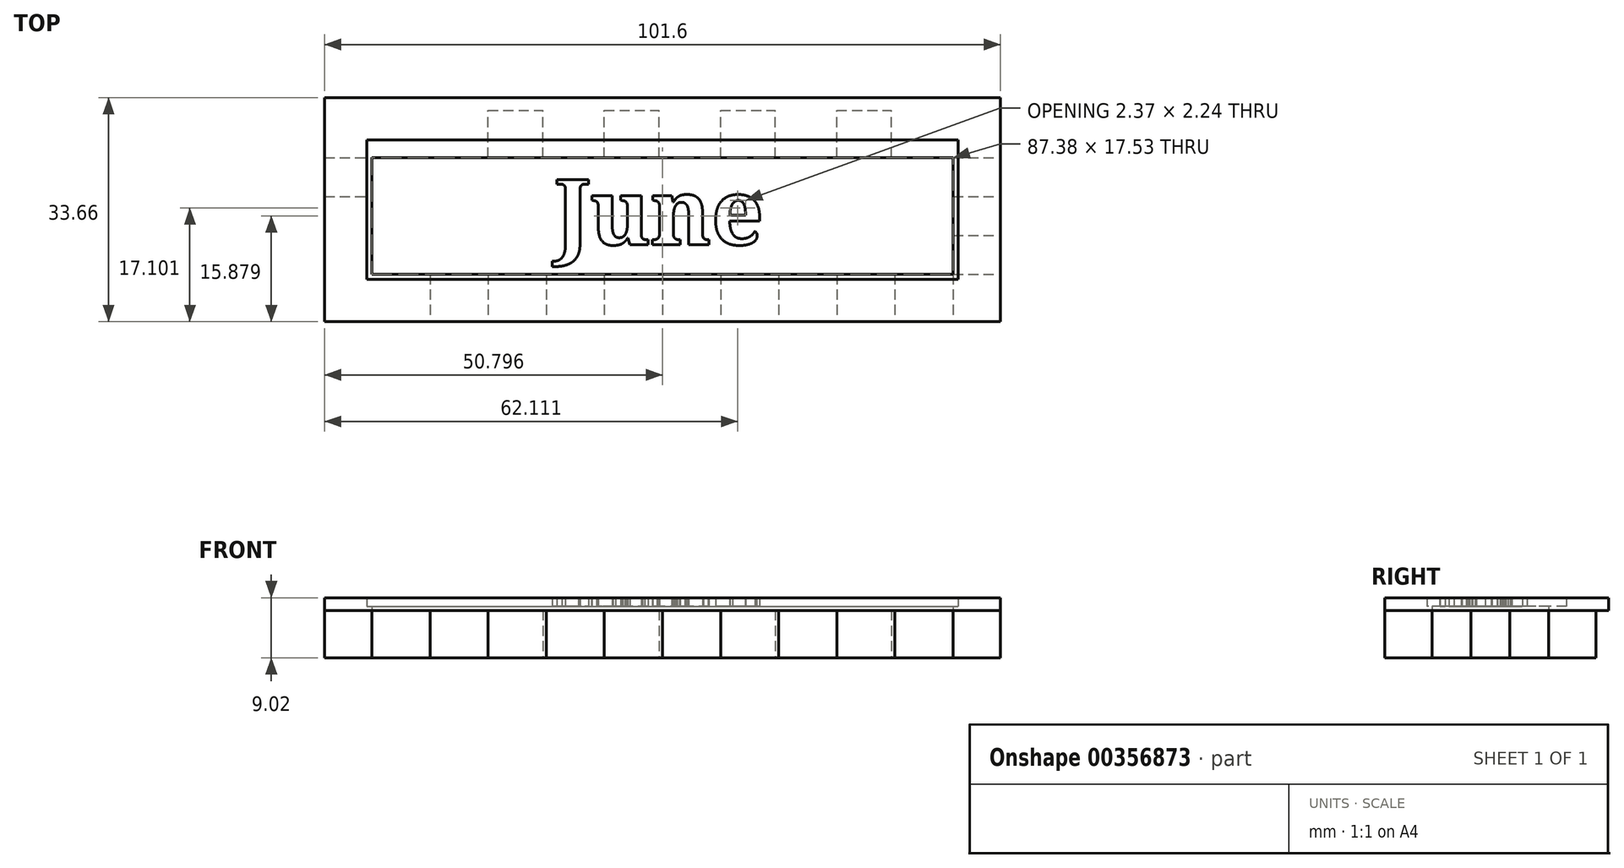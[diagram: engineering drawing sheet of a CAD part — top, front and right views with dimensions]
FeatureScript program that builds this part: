
annotation { "Feature Type Name" : "Feature", "Feature Type Description" : "" }
export const myFeature = defineFeature(function(context is Context, id is Id, definition is map)
    precondition{}
    {
        {
            var Q0;
            Q0=qCreatedBy(makeId("Top.planeOp"),FACE);
            var sketch = newSketch(context, id + "F0", { "sketchPlane" : qUnion([Q0])});
            skLineSegment(sketch, "E0.bottom", {"start": v(-52.12, 11.37) * mm, "end": v(49.48, 11.37) * mm});
            skLineSegment(sketch, "E0.top", {"start": v(-52.12, -20.38) * mm, "end": v(49.48, -20.38) * mm});
            skLineSegment(sketch, "E0.left", {"start": v(-52.12, 11.37) * mm, "end": v(-52.12, -20.38) * mm});
            skLineSegment(sketch, "E0.right", {"start": v(49.48, 11.37) * mm, "end": v(49.48, -20.38) * mm});
            skLineSegment(sketch, "E1.bottom", {"start": v(-52.12, 11.37) * mm, "end": v(-45.01, 11.37) * mm});
            skLineSegment(sketch, "E1.top", {"start": v(-52.12, 4.26) * mm, "end": v(-45.01, 4.26) * mm});
            skLineSegment(sketch, "E1.left", {"start": v(-52.12, 11.37) * mm, "end": v(-52.12, 4.26) * mm});
            skLineSegment(sketch, "E1.right", {"start": v(-45.01, 11.37) * mm, "end": v(-45.01, 4.26) * mm});
            skLineSegment(sketch, "E2.bottom", {"start": v(-45.01, 11.37) * mm, "end": v(-36.78, 11.37) * mm});
            skLineSegment(sketch, "E2.top", {"start": v(-45.01, 4.26) * mm, "end": v(-36.78, 4.26) * mm});
            skLineSegment(sketch, "E2.right", {"start": v(-36.78, 11.37) * mm, "end": v(-36.78, 4.26) * mm});
            skLineSegment(sketch, "E3.bottom", {"start": v(-36.78, 4.26) * mm, "end": v(-27.54, 4.26) * mm});
            skLineSegment(sketch, "E3.top", {"start": v(-36.78, 11.37) * mm, "end": v(-27.54, 11.37) * mm});
            skLineSegment(sketch, "E3.left", {"start": v(-36.78, 4.26) * mm, "end": v(-36.78, 11.37) * mm});
            skLineSegment(sketch, "E3.right", {"start": v(-27.54, 4.26) * mm, "end": v(-27.54, 11.37) * mm});
            skLineSegment(sketch, "E4.bottom", {"start": v(-27.54, 4.26) * mm, "end": v(-19.3, 4.26) * mm});
            skLineSegment(sketch, "E4.top", {"start": v(-27.54, 11.37) * mm, "end": v(-19.3, 11.37) * mm});
            skLineSegment(sketch, "E4.right", {"start": v(-19.3, 4.26) * mm, "end": v(-19.3, 11.37) * mm});
            skLineSegment(sketch, "E5.bottom", {"start": v(-19.3, 4.26) * mm, "end": v(-10.06, 4.26) * mm});
            skLineSegment(sketch, "E5.top", {"start": v(-19.3, 11.37) * mm, "end": v(-10.06, 11.37) * mm});
            skLineSegment(sketch, "E5.right", {"start": v(-10.06, 4.26) * mm, "end": v(-10.06, 11.37) * mm});
            skLineSegment(sketch, "E6.bottom", {"start": v(-10.06, 4.26) * mm, "end": v(-10.06, 4.26) * mm});
            skLineSegment(sketch, "E6.top", {"start": v(-10.06, 11.37) * mm, "end": v(-10.06, 11.37) * mm});
            skLineSegment(sketch, "E7.bottom", {"start": v(-10.06, 4.26) * mm, "end": v(-1.83, 4.26) * mm});
            skLineSegment(sketch, "E7.top", {"start": v(-10.06, 11.37) * mm, "end": v(-1.83, 11.37) * mm});
            skLineSegment(sketch, "E7.right", {"start": v(-1.83, 4.26) * mm, "end": v(-1.83, 11.37) * mm});
            skLineSegment(sketch, "E8.bottom", {"start": v(-1.83, 4.26) * mm, "end": v(7.41, 4.26) * mm});
            skLineSegment(sketch, "E8.top", {"start": v(-1.83, 11.37) * mm, "end": v(7.41, 11.37) * mm});
            skLineSegment(sketch, "E8.right", {"start": v(7.41, 4.26) * mm, "end": v(7.41, 11.37) * mm});
            skLineSegment(sketch, "E9.bottom", {"start": v(7.41, 4.26) * mm, "end": v(15.64, 4.26) * mm});
            skLineSegment(sketch, "E9.top", {"start": v(7.41, 11.37) * mm, "end": v(15.64, 11.37) * mm});
            skLineSegment(sketch, "E9.right", {"start": v(15.64, 4.26) * mm, "end": v(15.64, 11.37) * mm});
            skLineSegment(sketch, "E10.bottom", {"start": v(15.64, 4.26) * mm, "end": v(24.89, 4.26) * mm});
            skLineSegment(sketch, "E10.top", {"start": v(15.64, 11.37) * mm, "end": v(24.89, 11.37) * mm});
            skLineSegment(sketch, "E10.right", {"start": v(24.89, 4.26) * mm, "end": v(24.89, 11.37) * mm});
            skLineSegment(sketch, "E11.bottom", {"start": v(24.89, 4.26) * mm, "end": v(24.89, 4.26) * mm});
            skLineSegment(sketch, "E11.top", {"start": v(24.89, 11.37) * mm, "end": v(24.89, 11.37) * mm});
            skLineSegment(sketch, "E12.bottom", {"start": v(24.89, 4.26) * mm, "end": v(33.12, 4.26) * mm});
            skLineSegment(sketch, "E12.top", {"start": v(24.89, 11.37) * mm, "end": v(33.12, 11.37) * mm});
            skLineSegment(sketch, "E12.right", {"start": v(33.12, 4.26) * mm, "end": v(33.12, 11.37) * mm});
            skLineSegment(sketch, "E13.bottom", {"start": v(33.12, 4.26) * mm, "end": v(42.36, 4.26) * mm});
            skLineSegment(sketch, "E13.top", {"start": v(33.12, 11.37) * mm, "end": v(42.36, 11.37) * mm});
            skLineSegment(sketch, "E13.right", {"start": v(42.36, 4.26) * mm, "end": v(42.36, 11.37) * mm});
            skLineSegment(sketch, "E14.bottom", {"start": v(42.36, 4.26) * mm, "end": v(49.48, 4.26) * mm});
            skLineSegment(sketch, "E14.top", {"start": v(42.36, 11.37) * mm, "end": v(49.48, 11.37) * mm});
            skLineSegment(sketch, "E14.right", {"start": v(49.48, 4.26) * mm, "end": v(49.48, 11.37) * mm});
            skLineSegment(sketch, "E15.bottom", {"start": v(-52.12, -20.38) * mm, "end": v(-45.01, -20.38) * mm});
            skLineSegment(sketch, "E15.top", {"start": v(-52.12, -13.26) * mm, "end": v(-45.01, -13.26) * mm});
            skLineSegment(sketch, "E15.left", {"start": v(-52.12, -20.38) * mm, "end": v(-52.12, -13.26) * mm});
            skLineSegment(sketch, "E15.right", {"start": v(-45.01, -20.38) * mm, "end": v(-45.01, -13.26) * mm});
            skLineSegment(sketch, "E16.bottom", {"start": v(-45.01, -13.26) * mm, "end": v(-45.01, -13.26) * mm});
            skLineSegment(sketch, "E16.top", {"start": v(-45.01, -20.38) * mm, "end": v(-45.01, -20.38) * mm});
            skLineSegment(sketch, "E16.left", {"start": v(-45.01, -13.26) * mm, "end": v(-45.01, -20.38) * mm});
            skLineSegment(sketch, "E16.right", {"start": v(-45.01, -13.26) * mm, "end": v(-45.01, -20.38) * mm});
            skLineSegment(sketch, "E17.bottom", {"start": v(-45.01, -13.26) * mm, "end": v(-36.27, -13.26) * mm});
            skLineSegment(sketch, "E17.top", {"start": v(-45.01, -20.38) * mm, "end": v(-36.27, -20.38) * mm});
            skLineSegment(sketch, "E17.right", {"start": v(-36.27, -13.26) * mm, "end": v(-36.27, -20.38) * mm});
            skLineSegment(sketch, "E18.bottom", {"start": v(-36.27, -13.26) * mm, "end": v(-36.27, -13.26) * mm});
            skLineSegment(sketch, "E18.top", {"start": v(-36.27, -20.38) * mm, "end": v(-36.27, -20.38) * mm});
            skLineSegment(sketch, "E19.bottom", {"start": v(-36.27, -13.26) * mm, "end": v(-27.54, -13.26) * mm});
            skLineSegment(sketch, "E19.top", {"start": v(-36.27, -20.38) * mm, "end": v(-27.54, -20.38) * mm});
            skLineSegment(sketch, "E19.right", {"start": v(-27.54, -13.26) * mm, "end": v(-27.54, -20.38) * mm});
            skLineSegment(sketch, "E20.bottom", {"start": v(-27.54, -13.26) * mm, "end": v(-18.8, -13.26) * mm});
            skLineSegment(sketch, "E20.top", {"start": v(-27.54, -20.38) * mm, "end": v(-18.8, -20.38) * mm});
            skLineSegment(sketch, "E20.right", {"start": v(-18.8, -13.26) * mm, "end": v(-18.8, -20.38) * mm});
            skLineSegment(sketch, "E21.bottom", {"start": v(-18.8, -13.26) * mm, "end": v(-10.06, -13.26) * mm});
            skLineSegment(sketch, "E21.top", {"start": v(-18.8, -20.38) * mm, "end": v(-10.06, -20.38) * mm});
            skLineSegment(sketch, "E21.right", {"start": v(-10.06, -13.26) * mm, "end": v(-10.06, -20.38) * mm});
            skLineSegment(sketch, "E22.bottom", {"start": v(-10.06, -13.26) * mm, "end": v(-1.32, -13.26) * mm});
            skLineSegment(sketch, "E22.top", {"start": v(-10.06, -20.38) * mm, "end": v(-1.32, -20.38) * mm});
            skLineSegment(sketch, "E22.right", {"start": v(-1.32, -13.26) * mm, "end": v(-1.32, -20.38) * mm});
            skLineSegment(sketch, "E23.bottom", {"start": v(-1.32, -13.26) * mm, "end": v(7.41, -13.26) * mm});
            skLineSegment(sketch, "E23.top", {"start": v(-1.32, -20.38) * mm, "end": v(7.41, -20.38) * mm});
            skLineSegment(sketch, "E23.right", {"start": v(7.41, -13.26) * mm, "end": v(7.41, -20.38) * mm});
            skLineSegment(sketch, "E24.bottom", {"start": v(7.41, -13.26) * mm, "end": v(16.15, -13.26) * mm});
            skLineSegment(sketch, "E24.top", {"start": v(7.41, -20.38) * mm, "end": v(16.15, -20.38) * mm});
            skLineSegment(sketch, "E24.right", {"start": v(16.15, -13.26) * mm, "end": v(16.15, -20.38) * mm});
            skLineSegment(sketch, "E25.bottom", {"start": v(16.15, -13.26) * mm, "end": v(24.89, -13.26) * mm});
            skLineSegment(sketch, "E25.top", {"start": v(16.15, -20.38) * mm, "end": v(24.89, -20.38) * mm});
            skLineSegment(sketch, "E25.right", {"start": v(24.89, -13.26) * mm, "end": v(24.89, -20.38) * mm});
            skLineSegment(sketch, "E26.bottom", {"start": v(24.89, -13.26) * mm, "end": v(33.63, -13.26) * mm});
            skLineSegment(sketch, "E26.top", {"start": v(24.89, -20.38) * mm, "end": v(33.63, -20.38) * mm});
            skLineSegment(sketch, "E26.right", {"start": v(33.63, -13.26) * mm, "end": v(33.63, -20.38) * mm});
            skLineSegment(sketch, "E27.bottom", {"start": v(33.63, -13.26) * mm, "end": v(42.36, -13.26) * mm});
            skLineSegment(sketch, "E27.top", {"start": v(33.63, -20.38) * mm, "end": v(42.36, -20.38) * mm});
            skLineSegment(sketch, "E27.right", {"start": v(42.36, -13.26) * mm, "end": v(42.36, -20.38) * mm});
            skLineSegment(sketch, "E28.bottom", {"start": v(42.36, -13.26) * mm, "end": v(49.48, -13.26) * mm});
            skLineSegment(sketch, "E28.top", {"start": v(42.36, -20.38) * mm, "end": v(49.48, -20.38) * mm});
            skLineSegment(sketch, "E28.right", {"start": v(49.48, -13.26) * mm, "end": v(49.48, -20.38) * mm});
            skLineSegment(sketch, "E29.top", {"start": v(-52.12, -1.58) * mm, "end": v(-45.01, -1.58) * mm});
            skLineSegment(sketch, "E29.left", {"start": v(-52.12, 4.26) * mm, "end": v(-52.12, -1.58) * mm});
            skLineSegment(sketch, "E29.right", {"start": v(-45.01, 4.26) * mm, "end": v(-45.01, -1.58) * mm});
            skLineSegment(sketch, "E30.top", {"start": v(-52.12, -7.42) * mm, "end": v(-45.01, -7.42) * mm});
            skLineSegment(sketch, "E30.left", {"start": v(-52.12, -1.58) * mm, "end": v(-52.12, -7.42) * mm});
            skLineSegment(sketch, "E30.right", {"start": v(-45.01, -1.58) * mm, "end": v(-45.01, -7.42) * mm});
            skLineSegment(sketch, "E31.bottom", {"start": v(-45.01, -7.42) * mm, "end": v(-52.12, -7.42) * mm});
            skLineSegment(sketch, "E31.top", {"start": v(-45.01, -13.26) * mm, "end": v(-52.12, -13.26) * mm});
            skLineSegment(sketch, "E31.left", {"start": v(-45.01, -7.42) * mm, "end": v(-45.01, -13.26) * mm});
            skLineSegment(sketch, "E31.right", {"start": v(-52.12, -7.42) * mm, "end": v(-52.12, -13.26) * mm});
            skLineSegment(sketch, "E32.top", {"start": v(42.36, -1.58) * mm, "end": v(49.48, -1.58) * mm});
            skLineSegment(sketch, "E32.left", {"start": v(42.36, 4.26) * mm, "end": v(42.36, -1.58) * mm});
            skLineSegment(sketch, "E32.right", {"start": v(49.48, 4.26) * mm, "end": v(49.48, -1.58) * mm});
            skLineSegment(sketch, "E33.top", {"start": v(42.36, -7.42) * mm, "end": v(49.48, -7.42) * mm});
            skLineSegment(sketch, "E33.left", {"start": v(42.36, -1.58) * mm, "end": v(42.36, -7.42) * mm});
            skLineSegment(sketch, "E33.right", {"start": v(49.48, -1.58) * mm, "end": v(49.48, -7.42) * mm});
            skLineSegment(sketch, "E34.left", {"start": v(42.36, -7.42) * mm, "end": v(42.36, -13.26) * mm});
            skLineSegment(sketch, "E34.right", {"start": v(49.48, -7.42) * mm, "end": v(49.48, -13.26) * mm});
            skSolve(sketch);
        }
        {
            var Q0;
            Q0=makeQuery(id+"F0.imprint","IMPRINT",FACE,{"disambiguationData":[TD([[makeQuery(id+"F0.imprint","IMPRINT",EDGE,{"derivedFrom":sQuery(id+"F0.wireOp",EDGE,"E2.top")}),-1.0]])]});
            var Q1;
            Q1=makeQuery(id+"F0.imprint","IMPRINT",FACE,{"disambiguationData":[TD([[makeQuery(id+"F0.imprint","IMPRINT",EDGE,{"derivedFrom":sQuery(id+"F0.wireOp",EDGE,"E2.bottom")}),-1.0]])]});
            var Q2;
            Q2=makeQuery(id+"F0.imprint","IMPRINT",FACE,{"disambiguationData":[TD([[makeQuery(id+"F0.imprint","IMPRINT",EDGE,{"derivedFrom":sQuery(id+"F0.wireOp",EDGE,"E4.bottom")}),1.0]])]});
            var Q3;
            Q3=makeQuery(id+"F0.imprint","IMPRINT",FACE,{"disambiguationData":[TD([[makeQuery(id+"F0.imprint","IMPRINT",EDGE,{"derivedFrom":sQuery(id+"F0.wireOp",EDGE,"E7.bottom")}),1.0]])]});
            var Q4;
            Q4=makeQuery(id+"F0.imprint","IMPRINT",FACE,{"disambiguationData":[TD([[makeQuery(id+"F0.imprint","IMPRINT",EDGE,{"derivedFrom":sQuery(id+"F0.wireOp",EDGE,"E9.bottom")}),1.0]])]});
            var Q5;
            Q5=makeQuery(id+"F0.imprint","IMPRINT",FACE,{"disambiguationData":[TD([[makeQuery(id+"F0.imprint","IMPRINT",EDGE,{"derivedFrom":sQuery(id+"F0.wireOp",EDGE,"E12.bottom")}),1.0]])]});
            var Q6;
            Q6=makeQuery(id+"F0.imprint","IMPRINT",FACE,{"disambiguationData":[TD([[makeQuery(id+"F0.imprint","IMPRINT",EDGE,{"derivedFrom":sQuery(id+"F0.wireOp",EDGE,"E14.bottom")}),-1.0]])]});
            var Q7;
            Q7=makeQuery(id+"F0.imprint","IMPRINT",FACE,{"disambiguationData":[TD([[makeQuery(id+"F0.imprint","IMPRINT",EDGE,{"derivedFrom":sQuery(id+"F0.wireOp",EDGE,"E33.top")}),-1.0]])]});
            var Q8;
            Q8=makeQuery(id+"F0.imprint","IMPRINT",FACE,{"disambiguationData":[TD([[makeQuery(id+"F0.imprint","IMPRINT",EDGE,{"derivedFrom":sQuery(id+"F0.wireOp",EDGE,"E27.bottom")}),-1.0]])]});
            var Q9;
            Q9=makeQuery(id+"F0.imprint","IMPRINT",FACE,{"disambiguationData":[TD([[makeQuery(id+"F0.imprint","IMPRINT",EDGE,{"derivedFrom":sQuery(id+"F0.wireOp",EDGE,"E25.bottom")}),-1.0]])]});
            var Q10;
            Q10=makeQuery(id+"F0.imprint","IMPRINT",FACE,{"disambiguationData":[TD([[makeQuery(id+"F0.imprint","IMPRINT",EDGE,{"derivedFrom":sQuery(id+"F0.wireOp",EDGE,"E23.bottom")}),-1.0]])]});
            var Q11;
            Q11=makeQuery(id+"F0.imprint","IMPRINT",FACE,{"disambiguationData":[TD([[makeQuery(id+"F0.imprint","IMPRINT",EDGE,{"derivedFrom":sQuery(id+"F0.wireOp",EDGE,"E21.bottom")}),-1.0]])]});
            var Q12;
            Q12=makeQuery(id+"F0.imprint","IMPRINT",FACE,{"disambiguationData":[TD([[makeQuery(id+"F0.imprint","IMPRINT",EDGE,{"derivedFrom":sQuery(id+"F0.wireOp",EDGE,"E19.bottom")}),-1.0]])]});
            var Q13;
            Q13=makeQuery(id+"F0.imprint","IMPRINT",FACE,{"disambiguationData":[TD([[makeQuery(id+"F0.imprint","IMPRINT",EDGE,{"derivedFrom":sQuery(id+"F0.wireOp",EDGE,"E31.bottom")}),1.0]])]});
            var Q14;
            Q14=makeQuery(id+"F0.imprint","IMPRINT",FACE,{"disambiguationData":[TD([[makeQuery(id+"F0.imprint","IMPRINT",EDGE,{"derivedFrom":sQuery(id+"F0.wireOp",EDGE,"E1.top")}),-1.0]])]});
            extrude(context, id + "F1", {"entities" : qUnion([Q0, Q1, Q2, Q3, Q4, Q5, Q6, Q7, Q8, Q9, Q10, Q11, Q12, Q13, Q14]), "depth" : 7.11 * mm});
        }
        {
            var Q0;
            Q0=makeQuery(id+"F1.opExtrude","CAP_FACE",FACE,{"disambiguationData":[OSD([sQuery(id+"F0.wireOp",EDGE,"E2.bottom"),sQuery(id+"F0.wireOp",EDGE,"E1.right"),sQuery(id+"F0.wireOp",EDGE,"E3.bottom"),sQuery(id+"F0.wireOp",EDGE,"E3.left"),sQuery(id+"F0.wireOp",EDGE,"E4.top"),sQuery(id+"F0.wireOp",EDGE,"E3.right"),sQuery(id+"F0.wireOp",EDGE,"E5.bottom"),sQuery(id+"F0.wireOp",EDGE,"E4.right"),sQuery(id+"F0.wireOp",EDGE,"E6.top"),sQuery(id+"F0.wireOp",EDGE,"E5.right"),sQuery(id+"F0.wireOp",EDGE,"E7.bottom"),sQuery(id+"F0.wireOp",EDGE,"E5.right"),sQuery(id+"F0.wireOp",EDGE,"E8.top"),sQuery(id+"F0.wireOp",EDGE,"E7.right"),sQuery(id+"F0.wireOp",EDGE,"E9.bottom"),sQuery(id+"F0.wireOp",EDGE,"E8.right"),sQuery(id+"F0.wireOp",EDGE,"E10.top"),sQuery(id+"F0.wireOp",EDGE,"E9.right"),sQuery(id+"F0.wireOp",EDGE,"E11.bottom"),sQuery(id+"F0.wireOp",EDGE,"E10.right"),sQuery(id+"F0.wireOp",EDGE,"E12.top"),sQuery(id+"F0.wireOp",EDGE,"E10.right"),sQuery(id+"F0.wireOp",EDGE,"E13.bottom"),sQuery(id+"F0.wireOp",EDGE,"E12.right"),sQuery(id+"F0.wireOp",EDGE,"E16.bottom"),sQuery(id+"F0.wireOp",EDGE,"E17.top"),sQuery(id+"F0.wireOp",EDGE,"E16.left"),sQuery(id+"F0.wireOp",EDGE,"E18.bottom"),sQuery(id+"F0.wireOp",EDGE,"E17.right"),sQuery(id+"F0.wireOp",EDGE,"E19.top"),sQuery(id+"F0.wireOp",EDGE,"E17.right"),sQuery(id+"F0.wireOp",EDGE,"E20.bottom"),sQuery(id+"F0.wireOp",EDGE,"E19.right"),sQuery(id+"F0.wireOp",EDGE,"E21.top"),sQuery(id+"F0.wireOp",EDGE,"E20.right"),sQuery(id+"F0.wireOp",EDGE,"E22.bottom"),sQuery(id+"F0.wireOp",EDGE,"E21.right"),sQuery(id+"F0.wireOp",EDGE,"E23.top"),sQuery(id+"F0.wireOp",EDGE,"E22.right"),sQuery(id+"F0.wireOp",EDGE,"E24.bottom"),sQuery(id+"F0.wireOp",EDGE,"E23.right"),sQuery(id+"F0.wireOp",EDGE,"E25.top"),sQuery(id+"F0.wireOp",EDGE,"E24.right"),sQuery(id+"F0.wireOp",EDGE,"E26.bottom"),sQuery(id+"F0.wireOp",EDGE,"E25.right"),sQuery(id+"F0.wireOp",EDGE,"E27.top"),sQuery(id+"F0.wireOp",EDGE,"E26.right"),sQuery(id+"F0.wireOp",EDGE,"E27.right"),sQuery(id+"F0.wireOp",EDGE,"E1.top"),sQuery(id+"F0.wireOp",EDGE,"E29.left"),sQuery(id+"F0.wireOp",EDGE,"E29.top"),sQuery(id+"F0.wireOp",EDGE,"E30.right"),sQuery(id+"F0.wireOp",EDGE,"E31.bottom"),sQuery(id+"F0.wireOp",EDGE,"E31.top"),sQuery(id+"F0.wireOp",EDGE,"E31.right"),sQuery(id+"F0.wireOp",EDGE,"E14.bottom"),sQuery(id+"F0.wireOp",EDGE,"E32.right"),sQuery(id+"F0.wireOp",EDGE,"E32.top"),sQuery(id+"F0.wireOp",EDGE,"E33.left"),sQuery(id+"F0.wireOp",EDGE,"E33.top"),sQuery(id+"F0.wireOp",EDGE,"E28.bottom"),sQuery(id+"F0.wireOp",EDGE,"E34.right")])],"isStart":false});
            var sketch = newSketch(context, id + "F2", { "sketchPlane" : qUnion([Q0])});
            skLineSegment(sketch, "E35.bottom", {"start": v(-52.12, -20.38) * mm, "end": v(-45.01, -20.38) * mm});
            skLineSegment(sketch, "E35.top", {"start": v(-52.12, 13.28) * mm, "end": v(-45.01, 13.28) * mm});
            skLineSegment(sketch, "E35.left", {"start": v(-52.12, -20.38) * mm, "end": v(-52.12, 13.28) * mm});
            skLineSegment(sketch, "E35.right", {"start": v(-45.01, -20.38) * mm, "end": v(-45.01, 13.28) * mm});
            skLineSegment(sketch, "E36.bottom", {"start": v(-52.12, -20.38) * mm, "end": v(49.48, -20.38) * mm});
            skLineSegment(sketch, "E36.top", {"start": v(-52.12, -13.26) * mm, "end": v(49.48, -13.26) * mm});
            skLineSegment(sketch, "E36.left", {"start": v(-52.12, -20.38) * mm, "end": v(-52.12, -13.26) * mm});
            skLineSegment(sketch, "E36.right", {"start": v(49.48, -20.38) * mm, "end": v(49.48, -13.26) * mm});
            skPoint(sketch, "E37.oppositeSnap0", {"position": v(42.36, -4.5) * mm});
            skLineSegment(sketch, "E37.bottom", {"start": v(49.48, -20.38) * mm, "end": v(42.36, -20.38) * mm});
            skLineSegment(sketch, "E37.top", {"start": v(49.48, 13.28) * mm, "end": v(42.36, 13.28) * mm});
            skLineSegment(sketch, "E37.left", {"start": v(49.48, -20.38) * mm, "end": v(49.48, 13.28) * mm});
            skLineSegment(sketch, "E37.right", {"start": v(42.36, -20.38) * mm, "end": v(42.36, 13.28) * mm});
            skLineSegment(sketch, "E38.bottom", {"start": v(-52.12, 13.28) * mm, "end": v(49.48, 13.28) * mm});
            skLineSegment(sketch, "E38.top", {"start": v(-52.12, 4.26) * mm, "end": v(49.48, 4.26) * mm});
            skLineSegment(sketch, "E38.left", {"start": v(-52.12, 13.28) * mm, "end": v(-52.12, 4.26) * mm});
            skLineSegment(sketch, "E38.right", {"start": v(49.48, 13.28) * mm, "end": v(49.48, 4.26) * mm});
            skSolve(sketch);
        }
        {
            var Q0;
            Q0=qSketchRegion(id+"F2",true);
            var Q1;
            {var subQ5=sQuery(id+"F2.wireOp",EDGE,"E36.top");var subQ10=sQuery(id+"F2.wireOp",EDGE,"E35.right");var subQ12=makeQuery(id+"F2.imprint","INTERSECT",VERTEX,{"derivedFrom":[makeQuery(id+"F1.opExtrude","CAP_EDGE",EDGE,{"disambiguationData":[OSD([sQuery(id+"F0.wireOp",EDGE,"E31.bottom")])],"isStart":false}),subQ10]});var subQ24=makeQuery(id+"F2.imprint","INTERSECT",VERTEX,{"derivedFrom":[subQ10,subQ5]});Q1=makeQuery(id+"F2.imprint","IMPRINT",FACE,{"disambiguationData":[TD([[makeQuery(id+"F2.imprint","IMPRINT",EDGE,{"disambiguationData":[TD([[subQ12,1.0],[subQ24,-1.0]])],"derivedFrom":subQ10}),-1.0]])]});}
            extrude(context, id + "F3", {"entities" : qUnion([Q0, Q1]), "depth" : 0.64 * mm});
        }
        {
            var Q0;
            Q0=makeQuery(id+"F3.opExtrude","CAP_FACE",FACE,{"disambiguationData":[OSD([sQuery(id+"F2.wireOp",EDGE,"E35.left"),sQuery(id+"F2.wireOp",EDGE,"E36.bottom"),sQuery(id+"F2.wireOp",EDGE,"E36.left"),sQuery(id+"F2.wireOp",EDGE,"E37.bottom"),sQuery(id+"F2.wireOp",EDGE,"E37.left"),sQuery(id+"F2.wireOp",EDGE,"E38.bottom"),sQuery(id+"F2.wireOp",EDGE,"E38.left"),sQuery(id+"F2.wireOp",EDGE,"E38.right")])],"isStart":false});
            var sketch = newSketch(context, id + "F4", { "sketchPlane" : qUnion([Q0])});
            skLineSegment(sketch, "E39.bottom", {"start": v(-52.12, 13.28) * mm, "end": v(49.48, 13.28) * mm});
            skLineSegment(sketch, "E39.top", {"start": v(-52.12, 6.93) * mm, "end": v(49.48, 6.93) * mm});
            skLineSegment(sketch, "E39.left", {"start": v(-52.12, 13.28) * mm, "end": v(-52.12, 6.93) * mm});
            skLineSegment(sketch, "E39.right", {"start": v(49.48, 13.28) * mm, "end": v(49.48, 6.93) * mm});
            skLineSegment(sketch, "E40.bottom", {"start": v(-52.12, 13.28) * mm, "end": v(-45.77, 13.28) * mm});
            skLineSegment(sketch, "E40.top", {"start": v(-52.12, -20.38) * mm, "end": v(-45.77, -20.38) * mm});
            skLineSegment(sketch, "E40.left", {"start": v(-52.12, 13.28) * mm, "end": v(-52.12, -20.38) * mm});
            skLineSegment(sketch, "E40.right", {"start": v(-45.77, 13.28) * mm, "end": v(-45.77, -20.38) * mm});
            skLineSegment(sketch, "E41.bottom", {"start": v(-52.12, -14.03) * mm, "end": v(49.48, -14.03) * mm});
            skLineSegment(sketch, "E41.top", {"start": v(-52.12, -20.38) * mm, "end": v(49.48, -20.38) * mm});
            skLineSegment(sketch, "E41.left", {"start": v(-52.12, -14.03) * mm, "end": v(-52.12, -20.38) * mm});
            skLineSegment(sketch, "E41.right", {"start": v(49.48, -14.03) * mm, "end": v(49.48, -20.38) * mm});
            skLineSegment(sketch, "E42.bottom", {"start": v(49.48, -20.38) * mm, "end": v(43.13, -20.38) * mm});
            skLineSegment(sketch, "E42.top", {"start": v(49.48, 13.28) * mm, "end": v(43.13, 13.28) * mm});
            skLineSegment(sketch, "E42.left", {"start": v(49.48, -20.38) * mm, "end": v(49.48, 13.28) * mm});
            skLineSegment(sketch, "E42.right", {"start": v(43.13, -20.38) * mm, "end": v(43.13, 13.28) * mm});
            skSolve(sketch);
        }
        {
            var Q0;
            Q0=qSketchRegion(id+"F4",true);
            extrude(context, id + "F5", {"entities" : qUnion([Q0]), "operationType" : NewBodyOperationType.ADD, "depth" : 1.27 * mm});
        }
        {
            var Q0;
            Q0=makeQuery(id+"F3.opExtrude","CAP_FACE",FACE,{"disambiguationData":[OSD([sQuery(id+"F2.wireOp",EDGE,"E35.left"),sQuery(id+"F2.wireOp",EDGE,"E36.bottom"),sQuery(id+"F2.wireOp",EDGE,"E36.left"),sQuery(id+"F2.wireOp",EDGE,"E37.bottom"),sQuery(id+"F2.wireOp",EDGE,"E37.left"),sQuery(id+"F2.wireOp",EDGE,"E38.bottom"),sQuery(id+"F2.wireOp",EDGE,"E38.left"),sQuery(id+"F2.wireOp",EDGE,"E38.right")])],"isStart":false});
            var sketch = newSketch(context, id + "F6", { "sketchPlane" : qUnion([Q0])});
            skText(sketch, "E43", { "text": "June", "fontName": "NotoSerif-Bold.ttf"});
            const initialGuessF6  = {"E43": [-0.01734, -0.0088, 1, 0, 0.00988]};
            skSetInitialGuess(sketch, initialGuessF6);
            skSolve(sketch);
        }
        {
            var Q0;
            Q0 = qSketchRegion(id + "F6", true);
            extrude(context, id + "F7", {"entities" : qUnion([Q0]), "operationType" : NewBodyOperationType.ADD, "depth" : 1.27 * mm});
        }
    });
